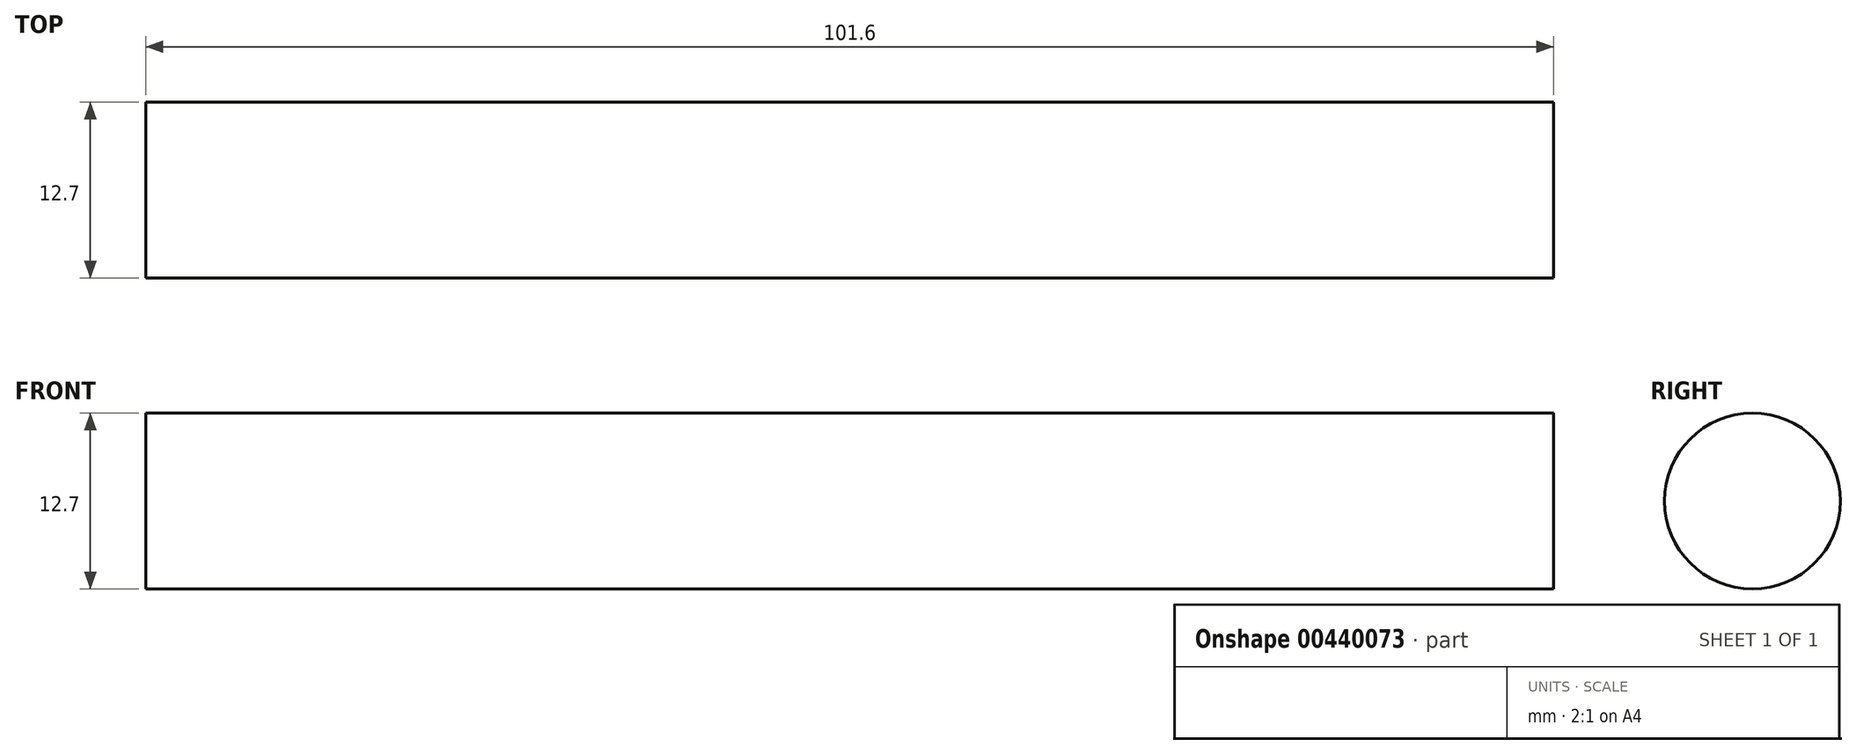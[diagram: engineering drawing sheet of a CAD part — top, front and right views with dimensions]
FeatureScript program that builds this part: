
annotation { "Feature Type Name" : "Feature", "Feature Type Description" : "" }
export const myFeature = defineFeature(function(context is Context, id is Id, definition is map)
    precondition{}
    {
        {
            var Q0;
            Q0=qCreatedBy(makeId("Right.planeOp"),FACE);
            var sketch = newSketch(context, id + "F0", { "sketchPlane" : qUnion([Q0])});
            skCircle(sketch, "E0", {"center": v(0, 0) * mm, "radius": 6.35 * mm});
            skSolve(sketch);
        }
        {
            var Q0;
            Q0 = qSketchRegion(id + "F0", true);
            extrude(context, id + "F1", {"entities" : qUnion([Q0]), "depth" : 101.6 * mm});
        }
    });
